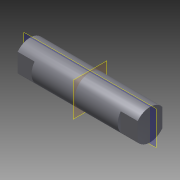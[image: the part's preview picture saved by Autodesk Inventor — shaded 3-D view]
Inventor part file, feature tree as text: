
AUTODESK INVENTOR PART (.ipt)
format: ipt  version: 2015 (Build 190159000, 159)  size: 99,840 bytes
history: native  units: mm
features: extrude x2, mirror x2, revolve x1
ambient origin geometry x8: Origin, YZ Plane, XZ Plane, XY Plane, X Axis, Y Axis, Z Axis, Center Point
bodies: Solid1 (feature_tree)
feature tree (5):
  revolve  "Revolución1"  [1 undecoded]
  extrude  "Extrusión3"  TaperAngle=90.0deg  [1 undecoded]
  mirror  "Simetría2"
  extrude  "Extrusión2"  Depth=10.0mm
  mirror  "Simetría1"
note: 2 required parameter values undecoded (feature->parameter linkage not recoverable at this tier; creation-order binding heuristic only, values carry confidence <= 0.55)